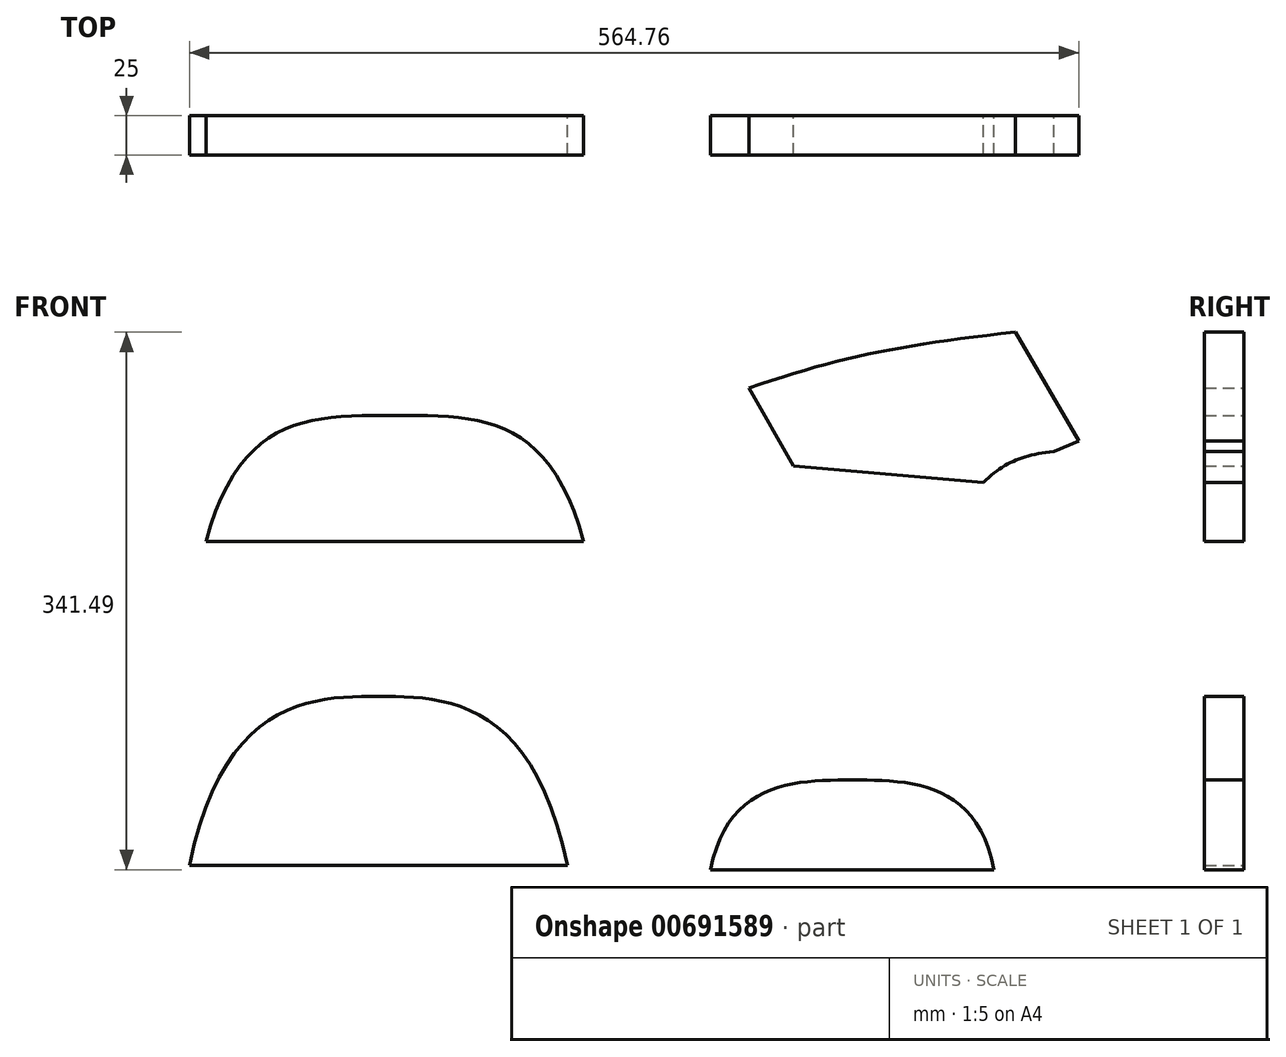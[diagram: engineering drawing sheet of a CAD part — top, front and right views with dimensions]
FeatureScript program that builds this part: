
annotation { "Feature Type Name" : "Feature", "Feature Type Description" : "" }
export const myFeature = defineFeature(function(context is Context, id is Id, definition is map)
    precondition{}
    {
        {
            var Q0;
            Q0=qCreatedBy(makeId("Front.planeOp"),FACE);
            var sketch = newSketch(context, id + "F0", { "sketchPlane" : qUnion([Q0])});
            skLineSegment(sketch, "E0", {"start": v(-209.73, 50.49) * mm, "end": v(-209.73, 130.49) * mm, "construction": true});
            skLineSegment(sketch, "E1", {"start": v(-329.73, 50.49) * mm, "end": v(-89.73, 50.49) * mm});
            skLineSegment(sketch, "E2", {"start": v(-307.55, 130.49) * mm, "end": v(-111.9, 130.49) * mm, "construction": true});
            skFitSpline(sketch, "E3", {"points": [v(-209.73, 130.49) * mm, v(-89.73, 50.49) * mm], "startDerivative": vector(165, 0) * mm, "endDerivative": vector(66.55, -240) * mm});
            skFitSpline(sketch, "E4", {"points": [v(-209.73, 130.49) * mm, v(-329.73, 50.49) * mm], "startDerivative": vector(-165, 0) * mm, "endDerivative": vector(-66.55, -240) * mm});
            skLineSegment(sketch, "E5", {"start": v(-220.13, -48.05) * mm, "end": v(-220.13, -155.52) * mm, "construction": true});
            skLineSegment(sketch, "E6", {"start": v(-318.4, -48.05) * mm, "end": v(-121.86, -48.05) * mm, "construction": true});
            skLineSegment(sketch, "E7", {"start": v(-340.13, -155.52) * mm, "end": v(-100.13, -155.52) * mm});
            skFitSpline(sketch, "E8", {"points": [v(-340.13, -155.52) * mm, v(-220.13, -48.05) * mm], "startDerivative": vector(65.17, 322.4) * mm, "endDerivative": vector(120, 0) * mm});
            skFitSpline(sketch, "E9", {"points": [v(-220.13, -48.05) * mm, v(-100.13, -155.52) * mm], "startDerivative": vector(120, 0) * mm, "endDerivative": vector(65.17, -322.4) * mm});
            skLineSegment(sketch, "E10", {"start": v(170.92, -158.18) * mm, "end": v(-9.08, -158.18) * mm});
            skLineSegment(sketch, "E11", {"start": v(80.92, -158.18) * mm, "end": v(80.92, -101.18) * mm, "construction": true});
            skLineSegment(sketch, "E12", {"start": v(1.8, -101.18) * mm, "end": v(160.05, -101.18) * mm, "construction": true});
            skFitSpline(sketch, "E13", {"points": [v(80.92, -101.18) * mm, v(170.92, -158.18) * mm], "startDerivative": vector(105, 0) * mm, "endDerivative": vector(32.62, -171) * mm});
            skFitSpline(sketch, "E14", {"points": [v(-9.08, -158.18) * mm, v(80.92, -101.18) * mm], "startDerivative": vector(32.62, 171) * mm, "endDerivative": vector(105, 0) * mm});
            skLineSegment(sketch, "E15", {"start": v(224.63, 114.03) * mm, "end": v(184.63, 183.31) * mm});
            skLineSegment(sketch, "E16", {"start": v(43.63, 98.44) * mm, "end": v(164.17, 87.9) * mm});
            skLineSegment(sketch, "E17", {"start": v(43.63, 98.44) * mm, "end": v(15.13, 147.8) * mm});
            skFitSpline(sketch, "E18", {"points": [v(15.13, 147.8) * mm, v(184.63, 183.31) * mm], "startDerivative": vector(171.13, 58.84) * mm, "endDerivative": vector(216.69, 23.06) * mm});
            skFitSpline(sketch, "E19", {"points": [v(164.17, 87.9) * mm, v(208.87, 107.66) * mm], "startDerivative": vector(39.64, 38.44) * mm, "endDerivative": vector(60.06, 7.2) * mm});
            skLineSegment(sketch, "E20", {"start": v(208.87, 107.66) * mm, "end": v(224.63, 114.03) * mm});
            skLineSegment(sketch, "E21", {"start": v(224.63, 114.03) * mm, "end": v(34.63, 114.03) * mm, "construction": true});
            skLineSegment(sketch, "E22", {"start": v(95.09, 170.22) * mm, "end": v(164.17, 87.9) * mm, "construction": true});
            skPoint(sketch, "E23", {"position": v(142.24, 114.03) * mm});
            skSolve(sketch);
        }
        {
            var Q0;
            Q0 = qSketchRegion(id + "F0", true);
            extrude(context, id + "F1", {"entities" : qUnion([Q0]), "depth" : 25 * mm, "offsetDistance" : 25 * mm});
        }
    });
